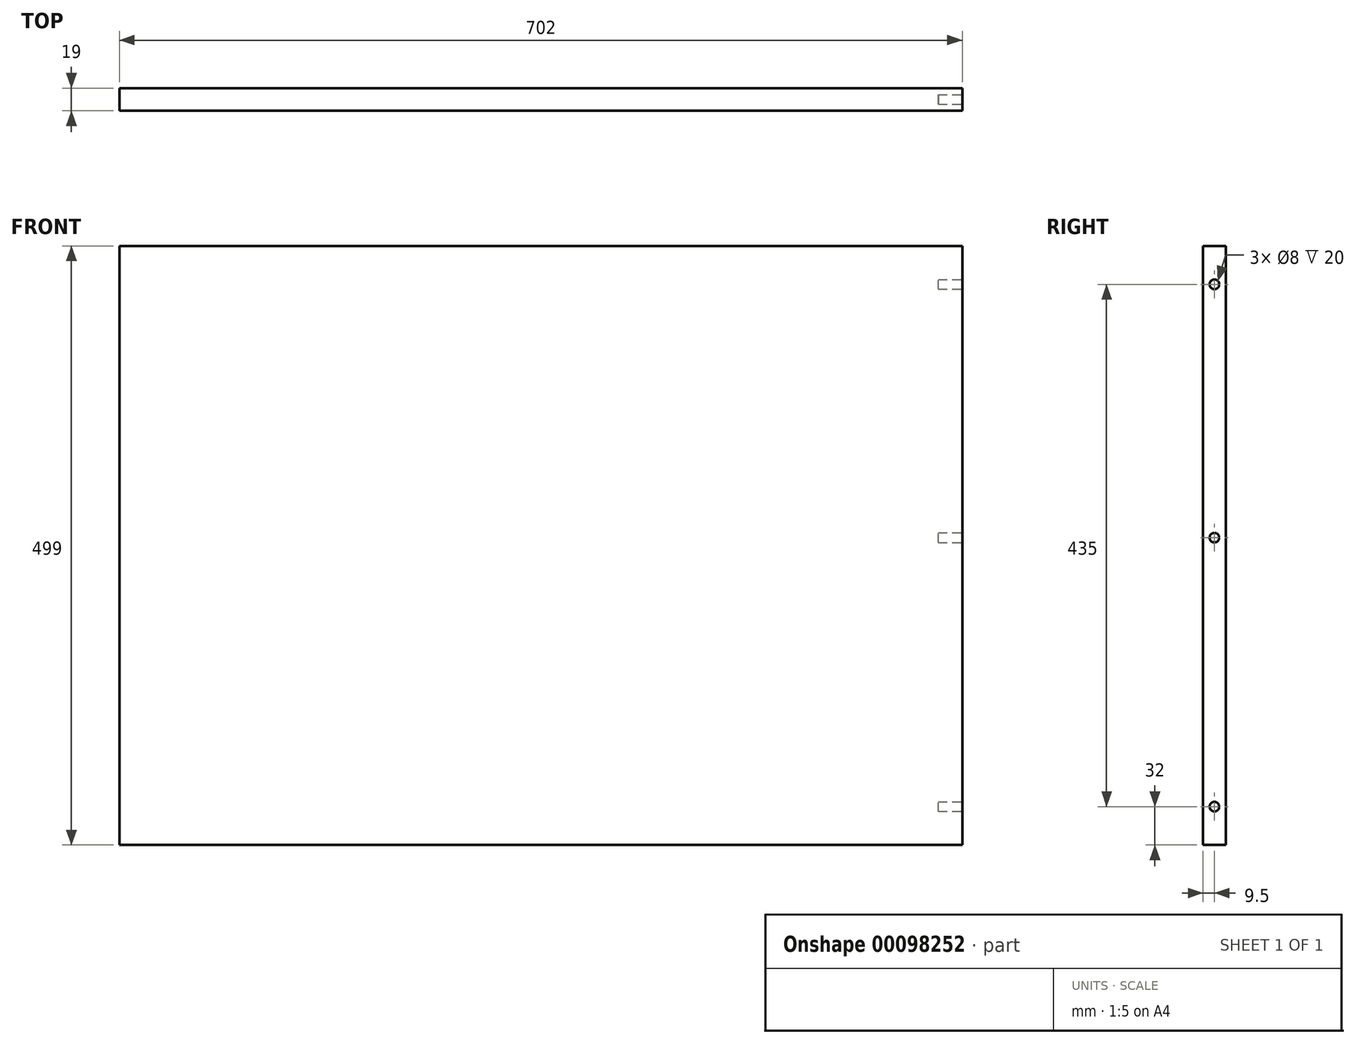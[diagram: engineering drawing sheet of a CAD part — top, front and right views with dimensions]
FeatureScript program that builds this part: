
annotation { "Feature Type Name" : "Feature", "Feature Type Description" : "" }
export const myFeature = defineFeature(function(context is Context, id is Id, definition is map)
    precondition{}
    {
        {
            var Q0;
            Q0=qCreatedBy(makeId("Front.planeOp"),FACE);
            var sketch = newSketch(context, id + "F0", { "sketchPlane" : qUnion([Q0])});
            skLineSegment(sketch, "E0.bottom", {"start": v(351, 249.5) * mm, "end": v(-351, 249.5) * mm});
            skLineSegment(sketch, "E0.top", {"start": v(351, -249.5) * mm, "end": v(-351, -249.5) * mm});
            skLineSegment(sketch, "E0.left", {"start": v(351, 249.5) * mm, "end": v(351, -249.5) * mm});
            skLineSegment(sketch, "E0.right", {"start": v(-351, 249.5) * mm, "end": v(-351, -249.5) * mm});
            skPoint(sketch, "E0.middle", {"position": v(0, 0) * mm});
            skSolve(sketch);
        }
        {
            var Q0;
            Q0 = qSketchRegion(id + "F0", true);
            extrude(context, id + "F1", {"entities" : qUnion([Q0]), "endBound" : BoundingType.SYMMETRIC, "depth" : 19 * mm});
        }
        {
            var Q0;
            Q0=makeQuery(id+"F1.opExtrude","SWEPT_FACE",FACE,{"disambiguationData":[OSD([sQuery(id+"F0.wireOp",EDGE,"E0.left")])]});
            var sketch = newSketch(context, id + "F2", { "sketchPlane" : qUnion([Q0])});
            skCircle(sketch, "E1", {"center": v(0, 217.5) * mm, "radius": 4 * mm});
            skCircle(sketch, "E2", {"center": v(0, 6.5) * mm, "radius": 4 * mm});
            skCircle(sketch, "E3", {"center": v(0, -217.5) * mm, "radius": 4 * mm});
            skLineSegment(sketch, "E4", {"start": v(0, 249.5) * mm, "end": v(0, 217.5) * mm, "construction": true});
            skLineSegment(sketch, "E5", {"start": v(0, 217.5) * mm, "end": v(0, 6.5) * mm, "construction": true});
            skLineSegment(sketch, "E6", {"start": v(0, 6.5) * mm, "end": v(0, -217.5) * mm, "construction": true});
            skLineSegment(sketch, "E7", {"start": v(0, -217.5) * mm, "end": v(0, -249.5) * mm, "construction": true});
            skSolve(sketch);
        }
        {
            var Q0;
            Q0 = qSketchRegion(id + "F2", true);
            extrude(context, id + "F3", {"entities" : qUnion([Q0]), "operationType" : NewBodyOperationType.REMOVE, "oppositeDirection" : true, "depth" : 20 * mm});
        }
    });
